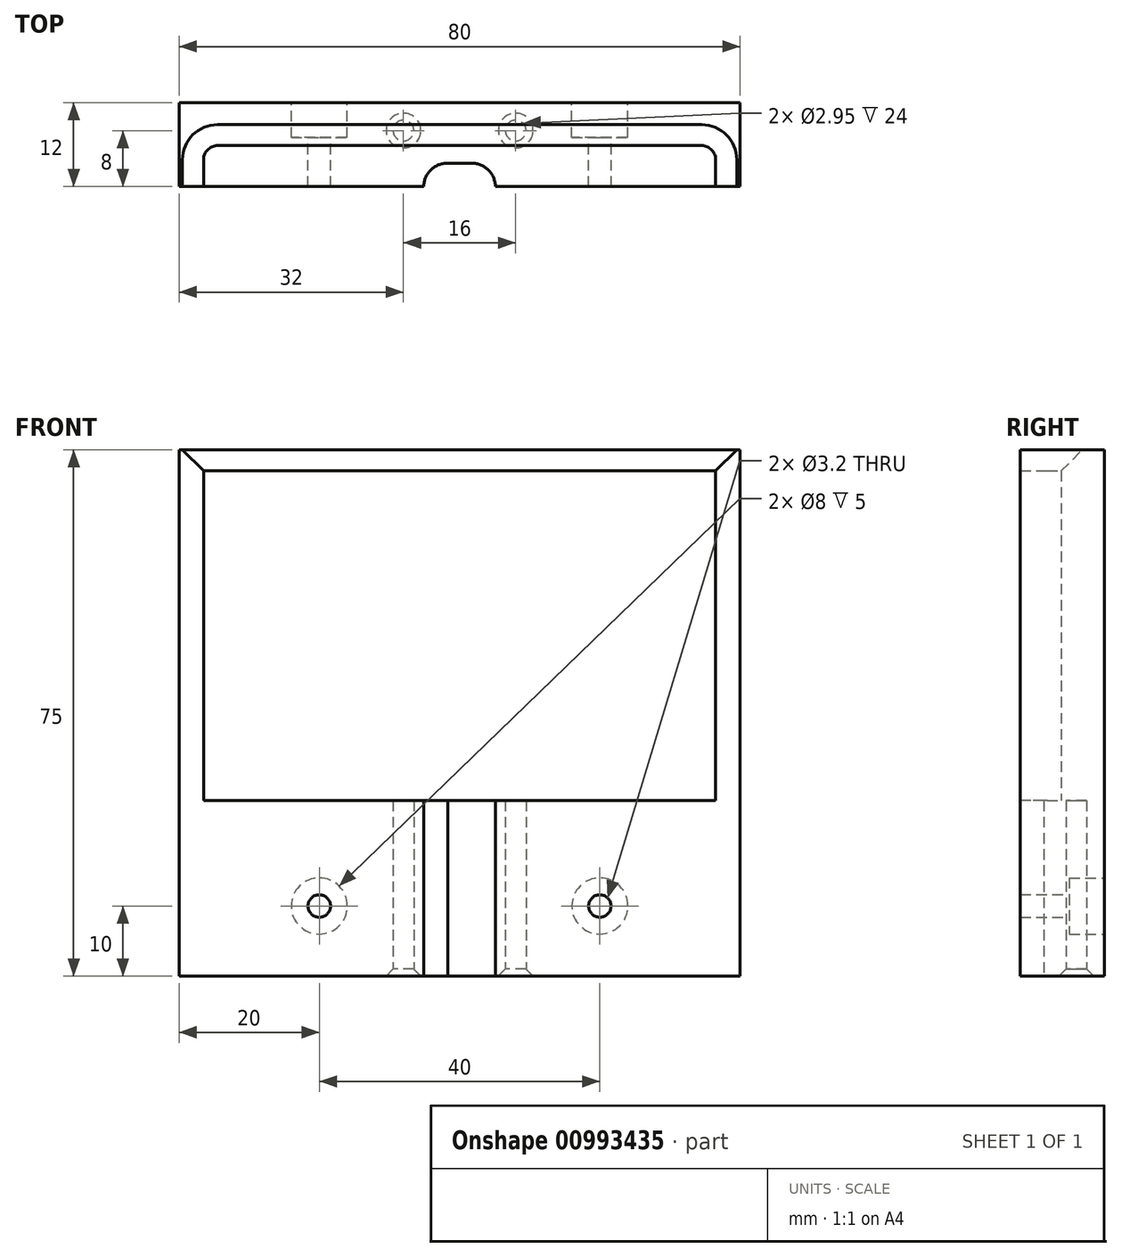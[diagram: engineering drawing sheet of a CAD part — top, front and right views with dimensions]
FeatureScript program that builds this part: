
annotation { "Feature Type Name" : "Feature", "Feature Type Description" : "" }
export const myFeature = defineFeature(function(context is Context, id is Id, definition is map)
    precondition{}
    {
        {
            var Q0;
            Q0=qCreatedBy(makeId("Top.planeOp"),FACE);
            var sketch = newSketch(context, id + "F0", { "sketchPlane" : qUnion([Q0])});
            skCircle(sketch, "E0", {"center": v(-1.75, 0) * mm, "radius": 3.35 * mm});
            skCircle(sketch, "E1", {"center": v(1.75, 0) * mm, "radius": 3.35 * mm});
            skLineSegment(sketch, "E2", {"start": v(-1.81, 3.35) * mm, "end": v(1.75, 3.35) * mm});
            skLineSegment(sketch, "E3", {"start": v(-1.79, -3.35) * mm, "end": v(1.75, -3.35) * mm});
            skPoint(sketch, "E4.middle", {"position": v(0, 0) * mm});
            skLineSegment(sketch, "E5.bottom", {"start": v(-40, 12) * mm, "end": v(40, 12) * mm});
            skLineSegment(sketch, "E5.left", {"start": v(-40, 12) * mm, "end": v(-40, 0) * mm});
            skLineSegment(sketch, "E5.right", {"start": v(40, 12) * mm, "end": v(40, 0) * mm});
            skLineSegment(sketch, "E6", {"start": v(-5.1, 0) * mm, "end": v(-40, 0) * mm});
            skLineSegment(sketch, "E7", {"start": v(5.1, 0) * mm, "end": v(40, 0) * mm});
            skCircle(sketch, "E8", {"center": v(-8, 8) * mm, "radius": 1.48 * mm});
            skCircle(sketch, "E9", {"center": v(8, 8) * mm, "radius": 1.48 * mm});
            skSolve(sketch);
        }
        {
            var Q0;
            Q0=makeQuery(id+"F0.imprint","IMPRINT",FACE,{"disambiguationData":[TD([[makeQuery(id+"F0.imprint","IMPRINT",EDGE,{"derivedFrom":sQuery(id+"F0.wireOp",EDGE,"E5.bottom")}),-1.0]])]});
            extrude(context, id + "F1", {"entities" : qUnion([Q0]), "depth" : 25 * mm, "offsetDistance" : 25 * mm});
        }
        {
            var Q0;
            Q0=makeQuery(id+"F1.opExtrude","SWEPT_FACE",FACE,{"disambiguationData":[OSD([sQuery(id+"F0.wireOp",EDGE,"E5.bottom")])]});
            var sketch = newSketch(context, id + "F2", { "sketchPlane" : qUnion([Q0])});
            skPoint(sketch, "E10", {"position": v(-20, 10) * mm});
            skPoint(sketch, "E11", {"position": v(20, 10) * mm});
            skCircle(sketch, "E12", {"center": v(-20, 10) * mm, "radius": 1.6 * mm});
            skCircle(sketch, "E13", {"center": v(20, 10) * mm, "radius": 1.6 * mm});
            skCircle(sketch, "E14", {"center": v(-20, 10) * mm, "radius": 4 * mm});
            skCircle(sketch, "E15", {"center": v(20, 10) * mm, "radius": 4 * mm});
            skSolve(sketch);
        }
        {
            var Q0;
            Q0=makeQuery(id+"F2.imprint","IMPRINT",FACE,{"disambiguationData":[TD([[makeQuery(id+"F2.imprint","IMPRINT",EDGE,{"derivedFrom":sQuery(id+"F2.wireOp",EDGE,"E12")}),1.0]])]});
            var Q1;
            Q1=makeQuery(id+"F2.imprint","IMPRINT",FACE,{"disambiguationData":[TD([[makeQuery(id+"F2.imprint","IMPRINT",EDGE,{"derivedFrom":sQuery(id+"F2.wireOp",EDGE,"E13")}),1.0]])]});
            extrude(context, id + "F3", {"entities" : qUnion([Q0, Q1]), "operationType" : NewBodyOperationType.REMOVE, "oppositeDirection" : true, "depth" : 30 * mm, "offsetDistance" : 25 * mm});
        }
        {
            var Q0;
            Q0=makeQuery(id+"F2.imprint","IMPRINT",FACE,{"disambiguationData":[TD([[makeQuery(id+"F2.imprint","IMPRINT",EDGE,{"derivedFrom":sQuery(id+"F2.wireOp",EDGE,"E12")}),-1.0]])]});
            var Q1;
            Q1=makeQuery(id+"F2.imprint","IMPRINT",FACE,{"disambiguationData":[TD([[makeQuery(id+"F2.imprint","IMPRINT",EDGE,{"derivedFrom":sQuery(id+"F2.wireOp",EDGE,"E13")}),-1.0]])]});
            extrude(context, id + "F4", {"entities" : qUnion([Q0, Q1]), "operationType" : NewBodyOperationType.REMOVE, "oppositeDirection" : true, "depth" : 5 * mm, "offsetDistance" : 25 * mm});
        }
        {
            var Q0;
            Q0=makeQuery(id+"F1.opExtrude","CAP_FACE",FACE,{"disambiguationData":[OSD([sQuery(id+"F0.wireOp",EDGE,"E0"),sQuery(id+"F0.wireOp",EDGE,"E1"),sQuery(id+"F0.wireOp",EDGE,"E2"),sQuery(id+"F0.wireOp",EDGE,"E5.bottom"),sQuery(id+"F0.wireOp",EDGE,"E5.left"),sQuery(id+"F0.wireOp",EDGE,"E5.right"),sQuery(id+"F0.wireOp",EDGE,"E6"),sQuery(id+"F0.wireOp",EDGE,"E7")])],"isStart":false});
            var sketch = newSketch(context, id + "F5", { "sketchPlane" : qUnion([Q0])});
            skLineSegment(sketch, "E16", {"start": v(-40, 12) * mm, "end": v(-40, 0) * mm});
            skLineSegment(sketch, "E17", {"start": v(-40, 0) * mm, "end": v(-36.5, 0) * mm});
            skLineSegment(sketch, "E18", {"start": v(-36.5, 0) * mm, "end": v(-36.5, 3.85) * mm});
            skLineSegment(sketch, "E19", {"start": v(-34.5, 5.85) * mm, "end": v(34.5, 5.85) * mm});
            skLineSegment(sketch, "E20", {"start": v(36.5, 3.85) * mm, "end": v(36.5, 0) * mm});
            skLineSegment(sketch, "E21", {"start": v(36.5, 0) * mm, "end": v(40, 0) * mm});
            skLineSegment(sketch, "E22", {"start": v(40, 0) * mm, "end": v(40, 12) * mm});
            skLineSegment(sketch, "E23", {"start": v(40, 12) * mm, "end": v(-40, 12) * mm});
            skPoint(sketch, "E24.visualSharp", {"position": v(-36.5, 5.85) * mm});
            skArc(sketch, "E24.filletArc", {"start": v(-34.5, 5.85) * mm, "mid": v(-35.91, 5.26) * mm, "end": v(-36.5, 3.85) * mm});
            skPoint(sketch, "E25.visualSharp", {"position": v(36.5, 5.85) * mm});
            skArc(sketch, "E25.filletArc", {"start": v(36.5, 3.85) * mm, "mid": v(35.91, 5.26) * mm, "end": v(34.5, 5.85) * mm});
            skSolve(sketch);
        }
        {
            var Q0;
            Q0=makeQuery(id+"F5.imprint","IMPRINT",FACE,{"disambiguationData":[TD([[makeQuery(id+"F5.imprint","IMPRINT",EDGE,{"derivedFrom":sQuery(id+"F5.wireOp",EDGE,"E16")}),1.0]])]});
            var Q1;
            Q1=makeQuery(id+"F5.imprint","IMPRINT",FACE,{"disambiguationData":[TD([[makeQuery(id+"F5.imprint","IMPRINT",EDGE,{"derivedFrom":makeQuery(id+"F1.opExtrude","CAP_EDGE",EDGE,{"disambiguationData":[OSD([sQuery(id+"F0.wireOp",EDGE,"E8")])],"isStart":false})}),1.0]])]});
            var Q2;
            Q2=makeQuery(id+"F5.imprint","IMPRINT",FACE,{"disambiguationData":[TD([[makeQuery(id+"F5.imprint","IMPRINT",EDGE,{"derivedFrom":makeQuery(id+"F1.opExtrude","CAP_EDGE",EDGE,{"disambiguationData":[OSD([sQuery(id+"F0.wireOp",EDGE,"E9")])],"isStart":false})}),1.0]])]});
            extrude(context, id + "F6", {"entities" : qUnion([Q0, Q1, Q2]), "operationType" : NewBodyOperationType.ADD, "depth" : 50 * mm, "offsetDistance" : 25 * mm});
        }
        {
            var Q0;
            Q0=makeQuery(id+"F6.opExtrude","CAP_EDGE",EDGE,{"disambiguationData":[OSD([sQuery(id+"F5.wireOp",EDGE,"E19")])],"isStart":false});
            chamfer(context, id + "F7", {"entities" : qUnion([Q0]), "width" : 3 * mm, "tangentPropagation" : true});
        }
        {
            var Q0;
            Q0=makeQuery(id+"F0.imprint","IMPRINT",FACE,{"disambiguationData":[TD([[makeQuery(id+"F0.imprint","IMPRINT",EDGE,{"derivedFrom":sQuery(id+"F0.wireOp",EDGE,"E8")}),1.0]])]});
            var Q1;
            Q1=makeQuery(id+"F0.imprint","IMPRINT",FACE,{"disambiguationData":[TD([[makeQuery(id+"F0.imprint","IMPRINT",EDGE,{"derivedFrom":sQuery(id+"F0.wireOp",EDGE,"E9")}),1.0]])]});
            extrude(context, id + "F8", {"entities" : qUnion([Q0, Q1]), "operationType" : NewBodyOperationType.REMOVE, "depth" : 20 * mm, "offsetDistance" : 25 * mm});
        }
        {
            var Q0;
            Q0=makeQuery(id+"F1.opExtrude","CAP_EDGE",EDGE,{"disambiguationData":[OSD([sQuery(id+"F0.wireOp",EDGE,"E8")])],"isStart":true});
            var Q1;
            Q1=makeQuery(id+"F1.opExtrude","CAP_EDGE",EDGE,{"disambiguationData":[OSD([sQuery(id+"F0.wireOp",EDGE,"E9")])],"isStart":true});
            chamfer(context, id + "F9", {"entities" : qUnion([Q0, Q1]), "width" : 1 * mm, "tangentPropagation" : true});
        }
    });
